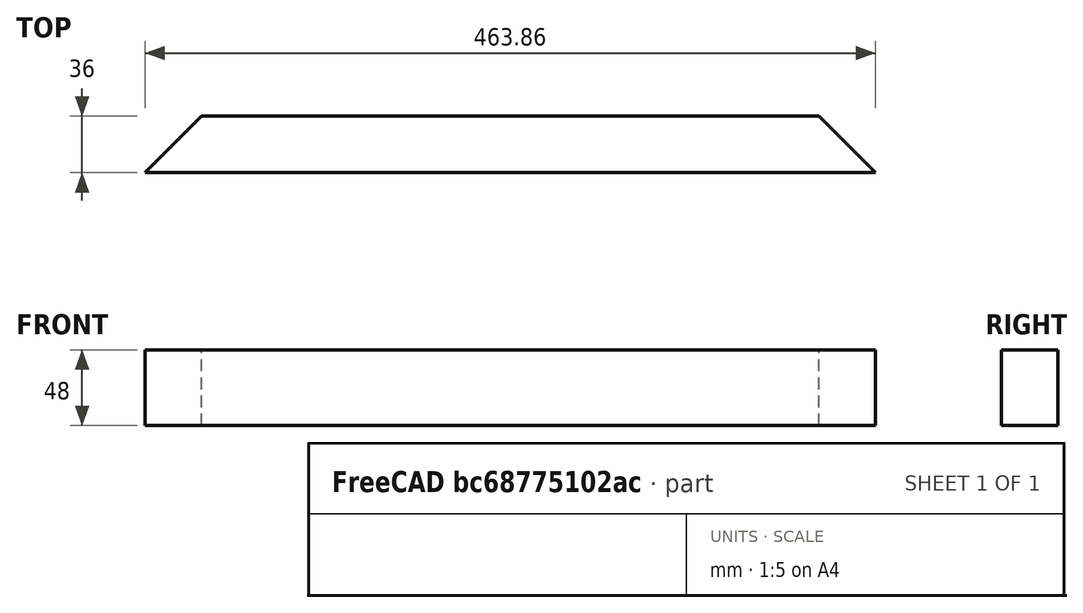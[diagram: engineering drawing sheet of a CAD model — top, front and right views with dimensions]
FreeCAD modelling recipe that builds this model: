
FCSTD DOCUMENT  (FreeCAD 0.19R24267 (Git))
Label: roofHipotenusa
License: Creative Commons Attribution-ShareAlike
LicenseURL: http://creativecommons.org/licenses/by-sa/4.0/
objects: Sketcher::SketchObject×1, Part::Extrusion×1
note: 2 computed .brp shape members not serialized (recipe doc carries the construction recipe); baked Part::Feature solids carry a one-line shape summary decoded from their .brp
EXTERNAL_REF file=Main.FCStd obj=Spreadsheet

FEATURE [Sketcher::SketchObject] Sketch001
  FullyConstrained = true
  expr: Constraints[8] = Main#<<params>>.structuralWoodHeight
  expr: Constraints[9] = Main#<<params>>.windowHeight - Main#<<params>>.hipotenusaStructuralWoodHeight * 2
  sketch-geometry (4):
    g0: LineSegment StartX=0 StartY=0 StartZ=0 EndX=36 EndY=36 EndZ=0
    g1: LineSegment StartX=36 StartY=36 StartZ=0 EndX=427.862 EndY=36 EndZ=0
    g2: LineSegment StartX=427.862 StartY=36 StartZ=0 EndX=463.862 EndY=0 EndZ=0
    g3: LineSegment StartX=463.862 StartY=0 StartZ=0 EndX=0 EndY=0 EndZ=0
  constraints (11):
    c: Coincident(g-1,g0)
    c: Coincident(g0,g1)
    c: Horizontal(g1)
    c: Coincident(g1,g2)
    c: PointOnObject(g2,g-1)
    c: Coincident(g2,g3)
    c: Coincident(g3,g0)
    c: Angle(g3,g0) = 0.785398
    c: DistanceY(g0,g0) = 36
    c: Distance(g3) = 463.862
    c: Equal(g0,g2)
FEATURE [Part::Extrusion] Extrude
  Base = -> Sketch001
  Dir = (0,0,1)
  DirMode = 2
  FaceMakerClass = Part::FaceMakerBullseye
  LengthFwd = 48
  LengthRev = 0
  Solid = true
  Symmetric = false
  expr: LengthFwd = Main#<<params>>.structuralWoodWidth
